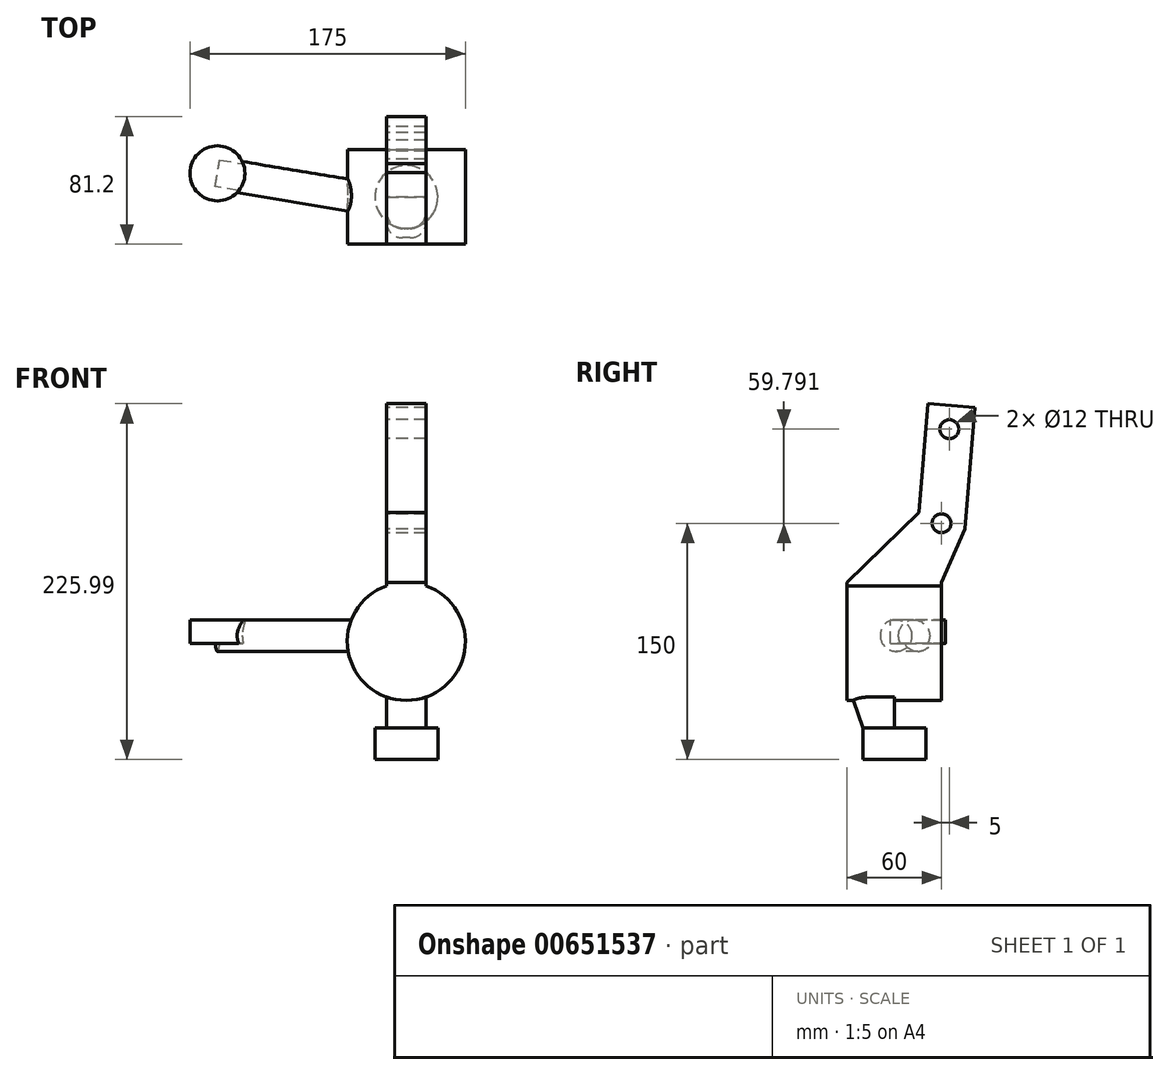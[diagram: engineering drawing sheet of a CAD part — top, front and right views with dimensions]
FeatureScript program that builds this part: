
annotation { "Feature Type Name" : "Feature", "Feature Type Description" : "" }
export const myFeature = defineFeature(function(context is Context, id is Id, definition is map)
    precondition{}
    {
        {
            var Q0;
            Q0=qCreatedBy(makeId("Front.planeOp"),FACE);
            var sketch = newSketch(context, id + "F0", { "sketchPlane" : qUnion([Q0])});
            skCircle(sketch, "E0", {"center": v(0, 0) * mm, "radius": 37.5 * mm});
            skSolve(sketch);
        }
        {
            var Q0;
            Q0=makeQuery(id+"F0.imprint","IMPRINT",FACE,{"disambiguationData":[TD([[makeQuery(id+"F0.imprint","IMPRINT",EDGE,{"derivedFrom":sQuery(id+"F0.wireOp",EDGE,"E0")}),1.0]])]});
            extrude(context, id + "F1", {"entities" : qUnion([Q0]), "endBound" : BoundingType.SYMMETRIC, "depth" : 60 * mm, "offsetDistance" : 25.4 * mm});
        }
        {
            var Q0;
            Q0=qCreatedBy(makeId("Top.planeOp"),FACE);
            cPlane(context, id + "F2", {"entities" : qUnion([Q0]), "cplaneType" : CPlaneType.OFFSET, "offset" : 75 * mm, "oppositeDirection" : true, "width" : 152.4 * mm, "height" : 152.4 * mm});
        }
        {
            var Q0;
            Q0=qCreatedBy(id+"F2.planeOp",FACE);
            var sketch = newSketch(context, id + "F3", { "sketchPlane" : qUnion([Q0])});
            skCircle(sketch, "E1", {"center": v(0, 0) * mm, "radius": 20 * mm});
            skSolve(sketch);
        }
        {
            var Q0;
            Q0=makeQuery(id+"F3.imprint","IMPRINT",FACE,{"disambiguationData":[TD([[makeQuery(id+"F3.imprint","IMPRINT",EDGE,{"derivedFrom":sQuery(id+"F3.wireOp",EDGE,"E1")}),1.0]])]});
            extrude(context, id + "F4", {"entities" : qUnion([Q0]), "depth" : 20 * mm, "offsetDistance" : 25.4 * mm});
        }
        {
            var Q0;
            Q0=qCreatedBy(makeId("Right.planeOp"),FACE);
            var sketch = newSketch(context, id + "F5", { "sketchPlane" : qUnion([Q0])});
            skLineSegment(sketch, "E2", {"start": v(-30, 37.5) * mm, "end": v(15.52, 81.84) * mm});
            skLineSegment(sketch, "E3", {"start": v(15.52, 81.84) * mm, "end": v(21.3, 150.99) * mm});
            skLineSegment(sketch, "E4", {"start": v(21.3, 150.99) * mm, "end": v(51.2, 148.49) * mm});
            skLineSegment(sketch, "E5", {"start": v(51.2, 148.49) * mm, "end": v(44.74, 71.28) * mm});
            skLineSegment(sketch, "E6", {"start": v(44.74, 71.28) * mm, "end": v(30, 37.5) * mm});
            skLineSegment(sketch, "E7", {"start": v(30, 37.5) * mm, "end": v(30, 25) * mm});
            skLineSegment(sketch, "E8", {"start": v(30, 25) * mm, "end": v(-30, 25) * mm});
            skLineSegment(sketch, "E9", {"start": v(-30, 25) * mm, "end": v(-30, 37.5) * mm});
            skLineSegment(sketch, "E10", {"start": v(-30, -25) * mm, "end": v(-20, -55) * mm});
            skLineSegment(sketch, "E11", {"start": v(-20, -55) * mm, "end": v(0, -55) * mm});
            skLineSegment(sketch, "E12", {"start": v(0, -55) * mm, "end": v(0, -25) * mm});
            skLineSegment(sketch, "E13", {"start": v(0, -25) * mm, "end": v(-30, -25) * mm});
            skCircle(sketch, "E14", {"center": v(35, 134.8) * mm, "radius": 6 * mm});
            skCircle(sketch, "E15", {"center": v(30, 75) * mm, "radius": 6 * mm});
            skLineSegment(sketch, "E16", {"start": v(36.25, 149.74) * mm, "end": v(35, 134.8) * mm, "construction": true});
            skLineSegment(sketch, "E17", {"start": v(35, 134.8) * mm, "end": v(20.05, 136.04) * mm, "construction": true});
            skLineSegment(sketch, "E18", {"start": v(35, 134.8) * mm, "end": v(49.95, 133.54) * mm, "construction": true});
            skLineSegment(sketch, "E19", {"start": v(30, 75) * mm, "end": v(43.75, 69) * mm, "construction": true});
            skSolve(sketch);
        }
        {
            var Q0;
            Q0=makeQuery(id+"F5.imprint","IMPRINT",FACE,{"disambiguationData":[TD([[makeQuery(id+"F5.imprint","IMPRINT",EDGE,{"derivedFrom":sQuery(id+"F5.wireOp",EDGE,"E2")}),-1.0]])]});
            var Q1;
            Q1=makeQuery(id+"F5.imprint","IMPRINT",FACE,{"disambiguationData":[TD([[makeQuery(id+"F5.imprint","IMPRINT",EDGE,{"derivedFrom":sQuery(id+"F5.wireOp",EDGE,"E10")}),1.0]])]});
            extrude(context, id + "F6", {"entities" : qUnion([Q0, Q1]), "operationType" : NewBodyOperationType.ADD, "endBound" : BoundingType.SYMMETRIC, "depth" : 25 * mm, "offsetDistance" : 25.4 * mm});
        }
        {
            var Q0;
            Q0=qCreatedBy(makeId("Top.planeOp"),FACE);
            cPlane(context, id + "F7", {"entities" : qUnion([Q0]), "cplaneType" : CPlaneType.OFFSET, "offset" : 13.72 * mm, "width" : 152.4 * mm, "height" : 152.4 * mm});
        }
        {
            var Q0;
            Q0=qCreatedBy(id+"F7.planeOp",FACE);
            var sketch = newSketch(context, id + "F8", { "sketchPlane" : qUnion([Q0])});
            skCircle(sketch, "E20", {"center": v(-120, 15) * mm, "radius": 17.5 * mm});
            skSolve(sketch);
        }
        {
            var Q0;
            Q0 = qSketchRegion(id + "F8", true);
            extrude(context, id + "F9", {"entities" : qUnion([Q0]), "operationType" : NewBodyOperationType.ADD, "oppositeDirection" : true, "depth" : 15 * mm, "offsetDistance" : 25.4 * mm});
        }
        {
            var Q0;
            Q0=qCreatedBy(id+"F7.planeOp",FACE);
            var sketch = newSketch(context, id + "F10", { "sketchPlane" : qUnion([Q0])});
            skLineSegment(sketch, "E21", {"start": v(-118.36, 24.86) * mm, "end": v(-28.36, 9.86) * mm});
            skLineSegment(sketch, "E22", {"start": v(-28.36, 9.86) * mm, "end": v(-31.64, -9.86) * mm});
            skLineSegment(sketch, "E23", {"start": v(-31.64, -9.86) * mm, "end": v(-121.64, 5.14) * mm});
            skLineSegment(sketch, "E24", {"start": v(-121.64, 5.14) * mm, "end": v(-118.36, 24.86) * mm});
            skPoint(sketch, "E25", {"position": v(-120, 15) * mm});
            skPoint(sketch, "E26", {"position": v(-30, 0) * mm});
            skSolve(sketch);
        }
        {
            var Q0;
            Q0=makeQuery(id+"F10.imprint","IMPRINT",FACE,{"disambiguationData":[TD([[makeQuery(id+"F10.imprint","IMPRINT",EDGE,{"derivedFrom":sQuery(id+"F10.wireOp",EDGE,"E21")}),-1.0]])]});
            extrude(context, id + "F11", {"entities" : qUnion([Q0]), "operationType" : NewBodyOperationType.ADD, "oppositeDirection" : true, "depth" : 20 * mm, "offsetDistance" : 25.4 * mm});
        }
        {
            var Q0;
            Q0=makeQuery(id+"F11.opExtrude","CAP_EDGE",EDGE,{"disambiguationData":[OSD([sQuery(id+"F10.wireOp",EDGE,"E23")])],"isStart":false});
            var Q1;
            Q1=makeQuery(id+"F11.opExtrude","CAP_EDGE",EDGE,{"disambiguationData":[OSD([sQuery(id+"F10.wireOp",EDGE,"E23")])],"isStart":true});
            var Q2;
            Q2=makeQuery(id+"F11.opExtrude","CAP_EDGE",EDGE,{"disambiguationData":[OSD([sQuery(id+"F10.wireOp",EDGE,"E21")])],"isStart":true});
            var Q3;
            Q3=makeQuery(id+"F11.opExtrude","CAP_EDGE",EDGE,{"disambiguationData":[OSD([sQuery(id+"F10.wireOp",EDGE,"E21")])],"isStart":false});
            fillet(context, id + "F12", {"entities" : qUnion([Q0, Q1, Q2, Q3]), "radius" : 10 * mm, "tangentPropagation" : true, "allowEdgeOverflow" : false});
        }
        {
            var Q0;
            Q0=makeQuery(id+"F6.opExtrude","CAP_EDGE",EDGE,{"disambiguationData":[OSD([sQuery(id+"F5.wireOp",EDGE,"E10")])],"isStart":false});
            var Q1;
            Q1=makeQuery(id+"F6.opExtrude","CAP_EDGE",EDGE,{"disambiguationData":[OSD([sQuery(id+"F5.wireOp",EDGE,"E10")])],"isStart":true});
            fillet(context, id + "F13", {"entities" : qUnion([Q0, Q1]), "radius" : 10 * mm, "tangentPropagation" : true, "allowEdgeOverflow" : false});
        }
    });
